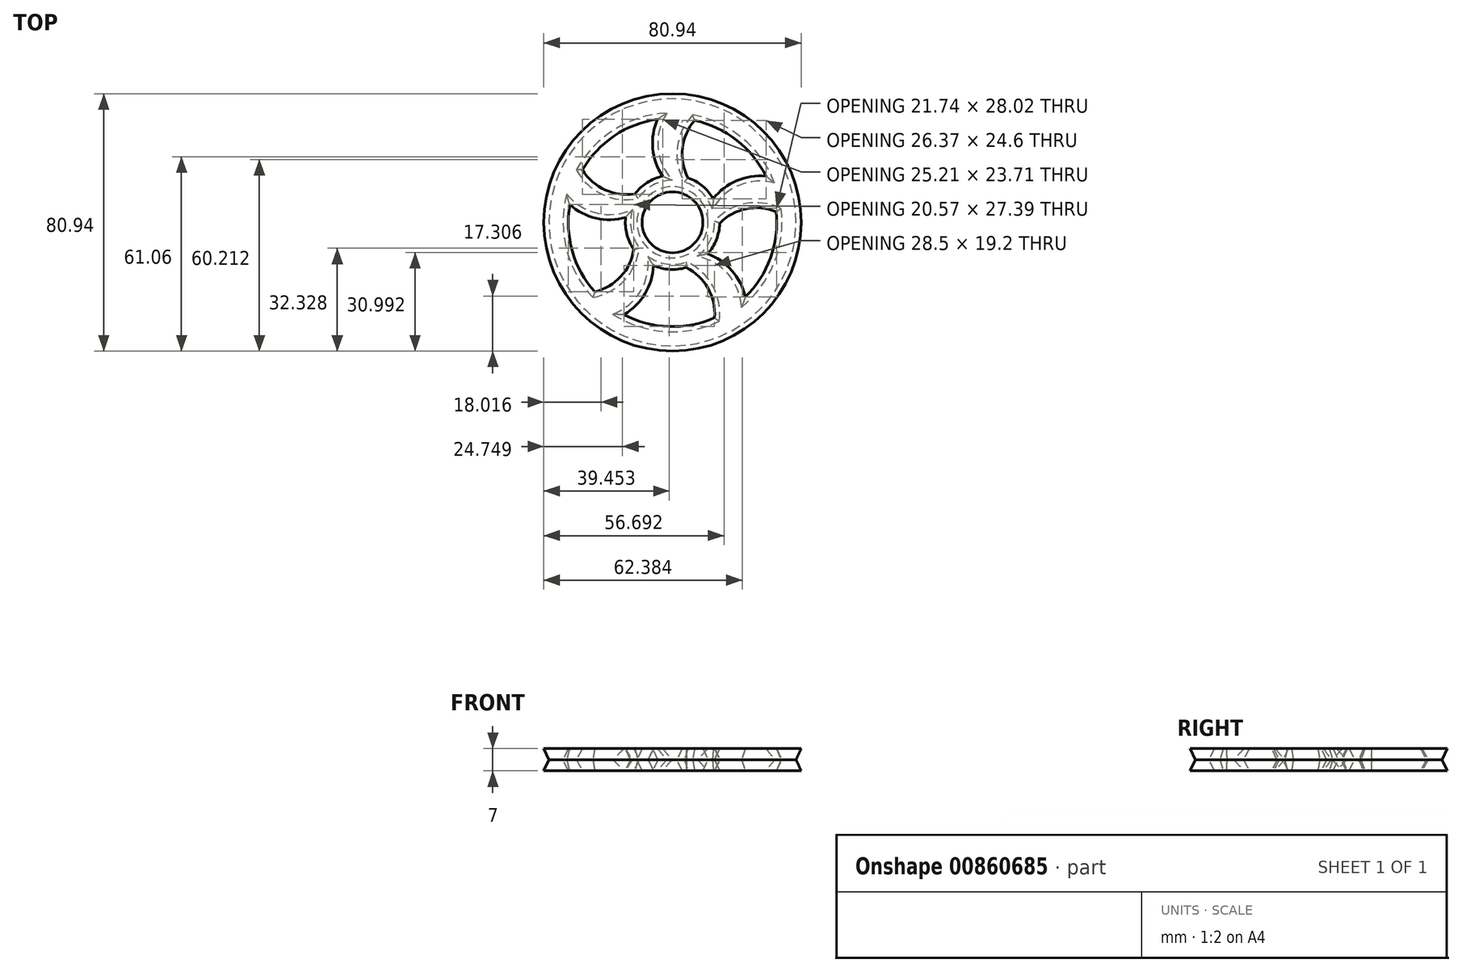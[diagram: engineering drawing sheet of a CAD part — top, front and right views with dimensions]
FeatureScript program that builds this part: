
annotation { "Feature Type Name" : "Feature", "Feature Type Description" : "" }
export const myFeature = defineFeature(function(context is Context, id is Id, definition is map)
    precondition{}
    {
        {
            var Q0;
            Q0=qCreatedBy(makeId("Top.planeOp"),FACE);
            var sketch = newSketch(context, id + "F0", { "sketchPlane" : qUnion([Q0])});
            skCircle(sketch, "E0", {"center": v(0, 0) * mm, "radius": 11.2 * mm});
            skCircle(sketch, "E1", {"center": v(0, 0) * mm, "radius": 13.2 * mm});
            skArc(sketch, "E2", {"start": v(0, 36.64) * mm, "mid": v(-4.65, 24.92) * mm, "end": v(0, 13.2) * mm});
            skArc(sketch, "E3", {"start": v(7.15, 34.59) * mm, "mid": v(1.6, 24.22) * mm, "end": v(3.74, 12.66) * mm});
            skArc(sketch, "E4.1.0", {"start": v(-34.85, 11.32) * mm, "mid": v(-25.14, 3.28) * mm, "end": v(-12.55, 4.08) * mm});
            skArc(sketch, "E4.1.1", {"start": v(-30.69, 17.49) * mm, "mid": v(-22.54, 9.01) * mm, "end": v(-10.88, 7.47) * mm});
            skArc(sketch, "E4.2.0", {"start": v(-21.54, -29.65) * mm, "mid": v(-10.89, -22.9) * mm, "end": v(-7.76, -10.68) * mm});
            skArc(sketch, "E4.2.1", {"start": v(-26.11, -23.78) * mm, "mid": v(-15.54, -18.65) * mm, "end": v(-10.47, -8.04) * mm});
            skArc(sketch, "E4.3.0", {"start": v(21.54, -29.65) * mm, "mid": v(18.4, -17.43) * mm, "end": v(7.76, -10.68) * mm});
            skArc(sketch, "E4.3.1", {"start": v(14.55, -32.18) * mm, "mid": v(12.94, -20.54) * mm, "end": v(4.41, -12.44) * mm});
            skArc(sketch, "E4.4.0", {"start": v(34.85, 11.32) * mm, "mid": v(22.27, 12.12) * mm, "end": v(12.55, 4.08) * mm});
            skArc(sketch, "E4.4.1", {"start": v(35.1, 3.9) * mm, "mid": v(23.53, 5.96) * mm, "end": v(13.2, 0.35) * mm});
            skCircle(sketch, "E5", {"center": v(0, 0) * mm, "radius": 34.42 * mm});
            skCircle(sketch, "E6", {"center": v(0, 0) * mm, "radius": 38.84 * mm});
            skSolve(sketch);
        }
        {
            var Q0;
            Q0=makeQuery(id+"F0.imprint","IMPRINT",FACE,{"disambiguationData":[TD([[makeQuery(id+"F0.imprint","IMPRINT",EDGE,{"derivedFrom":sQuery(id+"F0.wireOp",EDGE,"E0")}),-1.0]])]});
            var Q1;
            {var subQ0=sQuery(id+"F0.wireOp",EDGE,"E4.3.0");var subQ1=sQuery(id+"F0.wireOp",EDGE,"E1");var subQ2=makeQuery(id+"F0.imprint","INTERSECT",VERTEX,{"derivedFrom":[subQ1,subQ0]});Q1=makeQuery(id+"F0.imprint","IMPRINT",FACE,{"disambiguationData":[TD([[makeQuery(id+"F0.imprint","IMPRINT",EDGE,{"disambiguationData":[TD([[subQ2,1.0]])],"derivedFrom":subQ1}),-1.0]])]});}
            var Q2;
            {var subQ0=sQuery(id+"F0.wireOp",EDGE,"E4.1.0");var subQ1=sQuery(id+"F0.wireOp",EDGE,"E1");var subQ2=makeQuery(id+"F0.imprint","INTERSECT",VERTEX,{"derivedFrom":[subQ1,subQ0]});Q2=makeQuery(id+"F0.imprint","IMPRINT",FACE,{"disambiguationData":[TD([[makeQuery(id+"F0.imprint","IMPRINT",EDGE,{"disambiguationData":[TD([[subQ2,1.0]])],"derivedFrom":subQ1}),-1.0]])]});}
            var Q3;
            {var subQ0=sQuery(id+"F0.wireOp",EDGE,"E2");var subQ1=sQuery(id+"F0.wireOp",EDGE,"E1");var subQ2=makeQuery(id+"F0.imprint","INTERSECT",VERTEX,{"derivedFrom":[subQ1,subQ0]});Q3=makeQuery(id+"F0.imprint","IMPRINT",FACE,{"disambiguationData":[TD([[makeQuery(id+"F0.imprint","IMPRINT",EDGE,{"disambiguationData":[TD([[subQ2,1.0]])],"derivedFrom":subQ1}),-1.0]])]});}
            var Q4;
            Q4=makeQuery(id+"F0.imprint","IMPRINT",FACE,{"disambiguationData":[TD([[makeQuery(id+"F0.imprint","IMPRINT",EDGE,{"derivedFrom":sQuery(id+"F0.wireOp",EDGE,"E6")}),1.0]])]});
            var Q5;
            {var subQ0=sQuery(id+"F0.wireOp",EDGE,"E4.2.0");var subQ1=sQuery(id+"F0.wireOp",EDGE,"E1");var subQ2=makeQuery(id+"F0.imprint","INTERSECT",VERTEX,{"derivedFrom":[subQ1,subQ0]});Q5=makeQuery(id+"F0.imprint","IMPRINT",FACE,{"disambiguationData":[TD([[makeQuery(id+"F0.imprint","IMPRINT",EDGE,{"disambiguationData":[TD([[subQ2,1.0]])],"derivedFrom":subQ1}),-1.0]])]});}
            var Q6;
            {var subQ0=sQuery(id+"F0.wireOp",EDGE,"E4.4.0");var subQ1=sQuery(id+"F0.wireOp",EDGE,"E1");var subQ2=makeQuery(id+"F0.imprint","INTERSECT",VERTEX,{"derivedFrom":[subQ1,subQ0]});Q6=makeQuery(id+"F0.imprint","IMPRINT",FACE,{"disambiguationData":[TD([[makeQuery(id+"F0.imprint","IMPRINT",EDGE,{"disambiguationData":[TD([[subQ2,1.0]])],"derivedFrom":subQ1}),-1.0]])]});}
            extrude(context, id + "F1", {"entities" : qUnion([Q0, Q1, Q2, Q3, Q4, Q5, Q6]), "depth" : 7 * mm, "offsetDistance" : 25 * mm, "hasDraft" : true, "draftAngle" : 25 * degree, "hasSecondDirection" : true, "secondDirectionOppositeDirection" : true, "secondDirectionDepth" : 25 * mm, "symmetric" : true});
        }
    });
